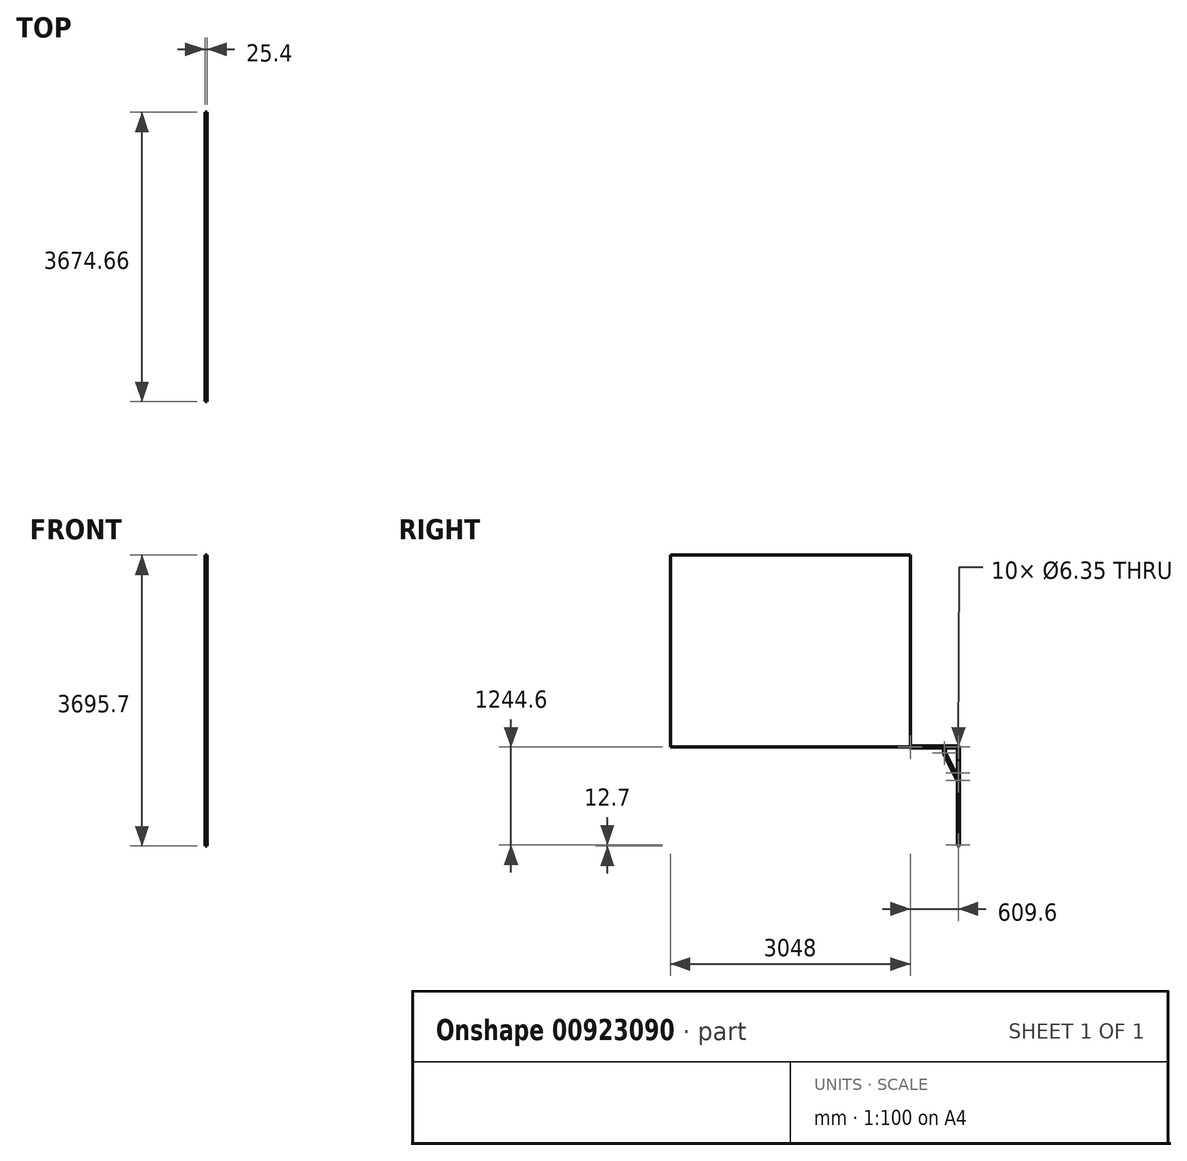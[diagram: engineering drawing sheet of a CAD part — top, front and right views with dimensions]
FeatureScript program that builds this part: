
annotation { "Feature Type Name" : "Feature", "Feature Type Description" : "" }
export const myFeature = defineFeature(function(context is Context, id is Id, definition is map)
    precondition{}
    {
        {
            var Q0;
            Q0=qCreatedBy(makeId("Right.planeOp"),FACE);
            var sketch = newSketch(context, id + "F0", { "sketchPlane" : qUnion([Q0])});
            skLineSegment(sketch, "E0.bottom", {"start": v(0, 0) * mm, "end": v(-3048, 0) * mm});
            skLineSegment(sketch, "E0.top", {"start": v(0, 2438.4) * mm, "end": v(-3048, 2438.4) * mm});
            skLineSegment(sketch, "E0.left", {"start": v(0, 0) * mm, "end": v(0, 2438.4) * mm});
            skLineSegment(sketch, "E0.right", {"start": v(-3048, 0) * mm, "end": v(-3048, 2438.4) * mm});
            skSolve(sketch);
        }
        {
            var Q0;
            Q0=makeQuery(id+"F0.imprint","IMPRINT",FACE,{"disambiguationData":[TD([[makeQuery(id+"F0.imprint","IMPRINT",EDGE,{"derivedFrom":sQuery(id+"F0.wireOp",EDGE,"E0.bottom")}),-1.0]])]});
            var sketch = newSketch(context, id + "F1", { "sketchPlane" : qUnion([Q0])});
            skLineSegment(sketch, "E1", {"start": v(0, 0) * mm, "end": v(609.6, 0) * mm, "construction": true});
            skLineSegment(sketch, "E2", {"start": v(609.6, -1244.6) * mm, "end": v(609.6, -330.2) * mm, "construction": true});
            skLineSegment(sketch, "E3", {"start": v(609.6, 0) * mm, "end": v(609.6, -330.2) * mm, "construction": true});
            skLineSegment(sketch, "E4", {"start": v(433.05, 0) * mm, "end": v(433.05, -76.2) * mm, "construction": true});
            skLineSegment(sketch, "E5", {"start": v(433.05, -76.2) * mm, "end": v(609.6, -425.39) * mm, "construction": true});
            skLineSegment(sketch, "E6.bottom", {"start": v(-12.7, 12.7) * mm, "end": v(622.3, 12.7) * mm});
            skLineSegment(sketch, "E6.top", {"start": v(-12.7, -12.7) * mm, "end": v(622.3, -12.7) * mm});
            skLineSegment(sketch, "E6.left", {"start": v(-12.7, 12.7) * mm, "end": v(-12.7, -12.7) * mm});
            skLineSegment(sketch, "E6.right", {"start": v(622.3, 12.7) * mm, "end": v(622.3, -12.7) * mm});
            skLineSegment(sketch, "E7.bottom", {"start": v(420.35, 0) * mm, "end": v(445.75, 0) * mm});
            skLineSegment(sketch, "E7.top", {"start": v(420.35, -88.9) * mm, "end": v(445.75, -88.9) * mm});
            skLineSegment(sketch, "E7.left", {"start": v(420.35, 0) * mm, "end": v(420.35, -88.9) * mm});
            skLineSegment(sketch, "E7.right", {"start": v(445.75, 0) * mm, "end": v(445.75, -88.9) * mm});
            skCircle(sketch, "E8", {"center": v(0, 0) * mm, "radius": 3.18 * mm});
            skCircle(sketch, "E9", {"center": v(433.05, -76.2) * mm, "radius": 3.18 * mm});
            skCircle(sketch, "E10", {"center": v(609.6, 0) * mm, "radius": 3.18 * mm});
            skLineSegment(sketch, "E11.bottom", {"start": v(596.9, -1257.3) * mm, "end": v(596.9, -317.5) * mm});
            skLineSegment(sketch, "E11.top", {"start": v(622.3, -1257.3) * mm, "end": v(622.3, -317.5) * mm});
            skLineSegment(sketch, "E11.left", {"start": v(596.9, -1257.3) * mm, "end": v(622.3, -1257.3) * mm});
            skLineSegment(sketch, "E11.right", {"start": v(596.9, -317.5) * mm, "end": v(622.3, -317.5) * mm});
            skLineSegment(sketch, "E12", {"start": v(438.66, -59.14) * mm, "end": v(626.66, -430.99) * mm});
            skLineSegment(sketch, "E13", {"start": v(626.66, -430.99) * mm, "end": v(604, -442.45) * mm});
            skLineSegment(sketch, "E14", {"start": v(604, -442.45) * mm, "end": v(415.99, -70.6) * mm});
            skLineSegment(sketch, "E15", {"start": v(415.99, -70.6) * mm, "end": v(438.66, -59.14) * mm});
            skCircle(sketch, "E16", {"center": v(609.6, -425.39) * mm, "radius": 3.18 * mm});
            skCircle(sketch, "E17", {"center": v(609.6, -1244.6) * mm, "radius": 3.18 * mm});
            skCircle(sketch, "E18", {"center": v(609.6, -330.2) * mm, "radius": 3.18 * mm});
            skLineSegment(sketch, "E19", {"start": v(622.3, 12.7) * mm, "end": v(622.3, -342.9) * mm});
            skLineSegment(sketch, "E20", {"start": v(622.3, -342.9) * mm, "end": v(596.9, -342.9) * mm});
            skLineSegment(sketch, "E21", {"start": v(596.9, -342.9) * mm, "end": v(596.9, 12.7) * mm});
            skLineSegment(sketch, "E22", {"start": v(596.9, 12.7) * mm, "end": v(622.3, 12.7) * mm});
            skSolve(sketch);
        }
        {
            var Q0;
            {var subQ6=sQuery(id+"F1.wireOp",EDGE,"E7.bottom");Q0=makeQuery(id+"F1.imprint","IMPRINT",FACE,{"disambiguationData":[TD([[makeQuery(id+"F1.imprint","IMPRINT",EDGE,{"derivedFrom":subQ6}),1.0]])]});}
            var Q1;
            Q1=makeQuery(id+"F1.imprint","IMPRINT",FACE,{"disambiguationData":[TD([[makeQuery(id+"F1.imprint","IMPRINT",EDGE,{"derivedFrom":sQuery(id+"F1.wireOp",EDGE,"E10")}),-1.0]])]});
            var Q2;
            {var subQ0=sQuery(id+"F1.wireOp",EDGE,"E6.right");var subQ1=sQuery(id+"F1.wireOp",EDGE,"E6.bottom");var subQ2=makeQuery(id+"F1.imprint","INTERSECT",VERTEX,{"derivedFrom":[subQ1,subQ0]});Q2=makeQuery(id+"F1.imprint","IMPRINT",FACE,{"disambiguationData":[TD([[makeQuery(id+"F1.imprint","IMPRINT",EDGE,{"disambiguationData":[TD([[subQ2,1.0]])],"derivedFrom":subQ1}),-1.0]])]});}
            var Q3;
            {var subQ0=sQuery(id+"F1.wireOp",EDGE,"E7.left");var subQ1=sQuery(id+"F1.wireOp",EDGE,"E6.top");var subQ2=makeQuery(id+"F1.imprint","INTERSECT",VERTEX,{"derivedFrom":[subQ1,subQ0]});Q3=makeQuery(id+"F1.imprint","IMPRINT",FACE,{"disambiguationData":[TD([[makeQuery(id+"F1.imprint","IMPRINT",EDGE,{"disambiguationData":[TD([[subQ2,-1.0]])],"derivedFrom":subQ1}),-1.0]])]});}
            var Q4;
            {var subQ5=sQuery(id+"F1.wireOp",EDGE,"E7.bottom");Q4=makeQuery(id+"F1.imprint","IMPRINT",FACE,{"disambiguationData":[TD([[makeQuery(id+"F1.imprint","IMPRINT",EDGE,{"derivedFrom":subQ5}),-1.0]])]});}
            var Q5;
            Q5=makeQuery(id+"F1.imprint","IMPRINT",FACE,{"disambiguationData":[TD([[makeQuery(id+"F1.imprint","IMPRINT",EDGE,{"derivedFrom":sQuery(id+"F1.wireOp",EDGE,"E9")}),-1.0]])]});
            var Q6;
            {var subQ0=sQuery(id+"F1.wireOp",EDGE,"E7.left");var subQ1=sQuery(id+"F1.wireOp",EDGE,"E7.top");var subQ2=makeQuery(id+"F1.imprint","INTERSECT",VERTEX,{"derivedFrom":[subQ1,subQ0]});Q6=makeQuery(id+"F1.imprint","IMPRINT",FACE,{"disambiguationData":[TD([[makeQuery(id+"F1.imprint","IMPRINT",EDGE,{"disambiguationData":[TD([[subQ2,-1.0]])],"derivedFrom":subQ1}),1.0]])]});}
            var Q7;
            {var subQ5=sQuery(id+"F1.wireOp",EDGE,"E6.left");var subQ6=sQuery(id+"F1.wireOp",EDGE,"E6.bottom");var subQ7=makeQuery(id+"F1.imprint","INTERSECT",VERTEX,{"derivedFrom":[subQ6,subQ5]});Q7=makeQuery(id+"F1.imprint","IMPRINT",FACE,{"disambiguationData":[TD([[makeQuery(id+"F1.imprint","IMPRINT",EDGE,{"disambiguationData":[TD([[subQ7,-1.0]])],"derivedFrom":subQ6}),-1.0]])]});}
            extrude(context, id + "F2", {"entities" : qUnion([Q0, Q1, Q2, Q3, Q4, Q5, Q6, Q7]), "depth" : 25.4 * mm, "offsetDistance" : 25.4 * mm});
        }
        {
            var Q0;
            {var subQ5=sQuery(id+"F1.wireOp",EDGE,"E7.right");var subQ7=sQuery(id+"F1.wireOp",EDGE,"E7.top");var subQ8=makeQuery(id+"F1.imprint","INTERSECT",VERTEX,{"derivedFrom":[subQ7,subQ5]});Q0=makeQuery(id+"F1.imprint","IMPRINT",FACE,{"disambiguationData":[TD([[makeQuery(id+"F1.imprint","IMPRINT",EDGE,{"disambiguationData":[TD([[subQ8,1.0]])],"derivedFrom":subQ7}),-1.0]])]});}
            var Q1;
            Q1=makeQuery(id+"F1.imprint","IMPRINT",FACE,{"disambiguationData":[TD([[makeQuery(id+"F1.imprint","IMPRINT",EDGE,{"derivedFrom":sQuery(id+"F1.wireOp",EDGE,"E9")}),-1.0]])]});
            var Q2;
            Q2=makeQuery(id+"F1.imprint","IMPRINT",FACE,{"disambiguationData":[TD([[makeQuery(id+"F1.imprint","IMPRINT",EDGE,{"derivedFrom":sQuery(id+"F1.wireOp",EDGE,"E16")}),-1.0]])]});
            var Q3;
            {var subQ0=sQuery(id+"F1.wireOp",EDGE,"E14");var subQ1=sQuery(id+"F1.wireOp",EDGE,"E11.top");var subQ2=makeQuery(id+"F1.imprint","INTERSECT",VERTEX,{"derivedFrom":[subQ1,subQ0]});Q3=makeQuery(id+"F1.imprint","IMPRINT",FACE,{"disambiguationData":[TD([[makeQuery(id+"F1.imprint","IMPRINT",EDGE,{"disambiguationData":[TD([[subQ2,-1.0]])],"derivedFrom":subQ1}),-1.0]])]});}
            var Q4;
            {var subQ0=sQuery(id+"F1.wireOp",EDGE,"E15");var subQ1=sQuery(id+"F1.wireOp",EDGE,"E7.left");var subQ2=makeQuery(id+"F1.imprint","INTERSECT",VERTEX,{"derivedFrom":[subQ1,subQ0]});Q4=makeQuery(id+"F1.imprint","IMPRINT",FACE,{"disambiguationData":[TD([[makeQuery(id+"F1.imprint","IMPRINT",EDGE,{"disambiguationData":[TD([[subQ2,-1.0]])],"derivedFrom":subQ1}),-1.0]])]});}
            extrude(context, id + "F3", {"entities" : qUnion([Q0, Q1, Q2, Q3, Q4]), "depth" : 25.4 * mm, "offsetDistance" : 25.4 * mm});
        }
        {
            var Q0;
            Q0=makeQuery(id+"F1.imprint","IMPRINT",FACE,{"disambiguationData":[TD([[makeQuery(id+"F1.imprint","IMPRINT",EDGE,{"derivedFrom":sQuery(id+"F1.wireOp",EDGE,"E10")}),-1.0]])]});
            var Q1;
            {var subQ0=sQuery(id+"F1.wireOp",EDGE,"E22");var subQ1=sQuery(id+"F1.wireOp",EDGE,"E6.bottom");var subQ2=makeQuery(id+"F1.imprint","INTERSECT",VERTEX,{"derivedFrom":[subQ1,subQ0]});Q1=makeQuery(id+"F1.imprint","IMPRINT",FACE,{"disambiguationData":[TD([[makeQuery(id+"F1.imprint","IMPRINT",EDGE,{"disambiguationData":[TD([[subQ2,-1.0]])],"derivedFrom":subQ1}),1.0]])]});}
            var Q2;
            {var subQ5=sQuery(id+"F1.wireOp",EDGE,"E6.right");var subQ6=sQuery(id+"F1.wireOp",EDGE,"E6.top");var subQ7=makeQuery(id+"F1.imprint","INTERSECT",VERTEX,{"derivedFrom":[subQ6,subQ5]});Q2=makeQuery(id+"F1.imprint","IMPRINT",FACE,{"disambiguationData":[TD([[makeQuery(id+"F1.imprint","IMPRINT",EDGE,{"disambiguationData":[TD([[subQ7,1.0]])],"derivedFrom":subQ6}),-1.0]])]});}
            var Q3;
            Q3=makeQuery(id+"F1.imprint","IMPRINT",FACE,{"disambiguationData":[TD([[makeQuery(id+"F1.imprint","IMPRINT",EDGE,{"derivedFrom":sQuery(id+"F1.wireOp",EDGE,"E18")}),-1.0]])]});
            var Q4;
            {var subQ0=sQuery(id+"F1.wireOp",EDGE,"E19");var subQ1=sQuery(id+"F1.wireOp",EDGE,"E11.right");var subQ2=makeQuery(id+"F1.imprint","INTERSECT",VERTEX,{"derivedFrom":[subQ1,subQ0]});Q4=makeQuery(id+"F1.imprint","IMPRINT",FACE,{"disambiguationData":[TD([[makeQuery(id+"F1.imprint","IMPRINT",EDGE,{"disambiguationData":[TD([[subQ2,-1.0]])],"derivedFrom":subQ1}),1.0]])]});}
            var Q5;
            {var subQ0=sQuery(id+"F1.wireOp",EDGE,"E21");var subQ1=sQuery(id+"F1.wireOp",EDGE,"E11.top");var subQ2=makeQuery(id+"F1.imprint","INTERSECT",VERTEX,{"derivedFrom":[subQ1,subQ0]});Q5=makeQuery(id+"F1.imprint","IMPRINT",FACE,{"disambiguationData":[TD([[makeQuery(id+"F1.imprint","IMPRINT",EDGE,{"disambiguationData":[TD([[subQ2,-1.0]])],"derivedFrom":subQ1}),-1.0]])]});}
            extrude(context, id + "F4", {"entities" : qUnion([Q0, Q1, Q2, Q3, Q4, Q5]), "depth" : 25.4 * mm, "offsetDistance" : 25.4 * mm});
        }
        {
            var Q0;
            {var subQ5=sQuery(id+"F1.wireOp",EDGE,"E11.left");Q0=makeQuery(id+"F1.imprint","IMPRINT",FACE,{"disambiguationData":[TD([[makeQuery(id+"F1.imprint","IMPRINT",EDGE,{"derivedFrom":subQ5}),1.0]])]});}
            var Q1;
            Q1=makeQuery(id+"F1.imprint","IMPRINT",FACE,{"disambiguationData":[TD([[makeQuery(id+"F1.imprint","IMPRINT",EDGE,{"derivedFrom":sQuery(id+"F1.wireOp",EDGE,"E16")}),-1.0]])]});
            var Q2;
            {var subQ1=sQuery(id+"F1.wireOp",EDGE,"E12");var subQ3=sQuery(id+"F1.wireOp",EDGE,"E11.bottom");var subQ4=makeQuery(id+"F1.imprint","INTERSECT",VERTEX,{"derivedFrom":[subQ3,subQ1]});Q2=makeQuery(id+"F1.imprint","IMPRINT",FACE,{"disambiguationData":[TD([[makeQuery(id+"F1.imprint","IMPRINT",EDGE,{"disambiguationData":[TD([[subQ4,-1.0]])],"derivedFrom":subQ3}),-1.0]])]});}
            var Q3;
            Q3=makeQuery(id+"F1.imprint","IMPRINT",FACE,{"disambiguationData":[TD([[makeQuery(id+"F1.imprint","IMPRINT",EDGE,{"derivedFrom":sQuery(id+"F1.wireOp",EDGE,"E18")}),-1.0]])]});
            var Q4;
            {var subQ0=sQuery(id+"F1.wireOp",EDGE,"E11.right");var subQ1=sQuery(id+"F1.wireOp",EDGE,"E11.top");var subQ2=makeQuery(id+"F1.imprint","INTERSECT",VERTEX,{"derivedFrom":[subQ1,subQ0]});Q4=makeQuery(id+"F1.imprint","IMPRINT",FACE,{"disambiguationData":[TD([[makeQuery(id+"F1.imprint","IMPRINT",EDGE,{"disambiguationData":[TD([[subQ2,1.0]])],"derivedFrom":subQ1}),1.0]])]});}
            var Q5;
            {var subQ0=sQuery(id+"F1.wireOp",EDGE,"E11.right");var subQ1=sQuery(id+"F1.wireOp",EDGE,"E11.bottom");var subQ2=makeQuery(id+"F1.imprint","INTERSECT",VERTEX,{"derivedFrom":[subQ1,subQ0]});Q5=makeQuery(id+"F1.imprint","IMPRINT",FACE,{"disambiguationData":[TD([[makeQuery(id+"F1.imprint","IMPRINT",EDGE,{"disambiguationData":[TD([[subQ2,1.0]])],"derivedFrom":subQ1}),-1.0]])]});}
            extrude(context, id + "F5", {"entities" : qUnion([Q0, Q1, Q2, Q3, Q4, Q5]), "depth" : 25.4 * mm, "offsetDistance" : 25.4 * mm});
        }
    });
